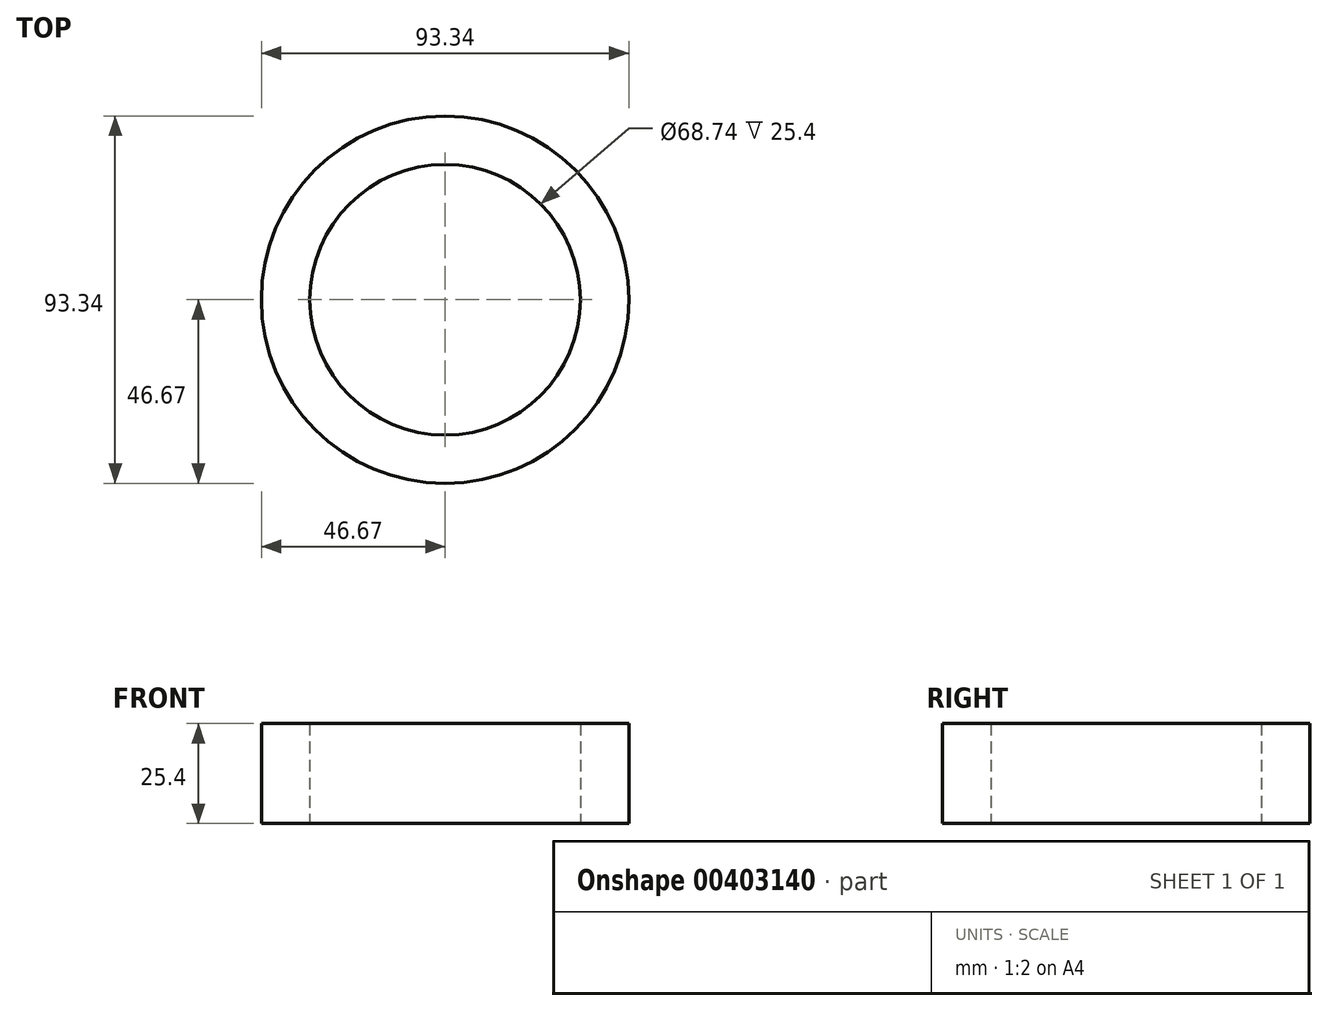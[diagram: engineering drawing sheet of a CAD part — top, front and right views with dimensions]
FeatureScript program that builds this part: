
annotation { "Feature Type Name" : "Feature", "Feature Type Description" : "" }
export const myFeature = defineFeature(function(context is Context, id is Id, definition is map)
    precondition{}
    {
        {
            var Q0;
            Q0=qCreatedBy(makeId("Top.planeOp"),FACE);
            var sketch = newSketch(context, id + "F0", { "sketchPlane" : qUnion([Q0])});
            skCircle(sketch, "E0", {"center": v(0, 0) * mm, "radius": 46.67 * mm});
            skCircle(sketch, "E1", {"center": v(0, 0) * mm, "radius": 34.37 * mm});
            skSolve(sketch);
        }
        {
            var Q0;
            Q0 = qSketchRegion(id + "F0", true);
            extrude(context, id + "F1", {"entities" : qUnion([Q0]), "depth" : 25.4 * mm});
        }
    });
